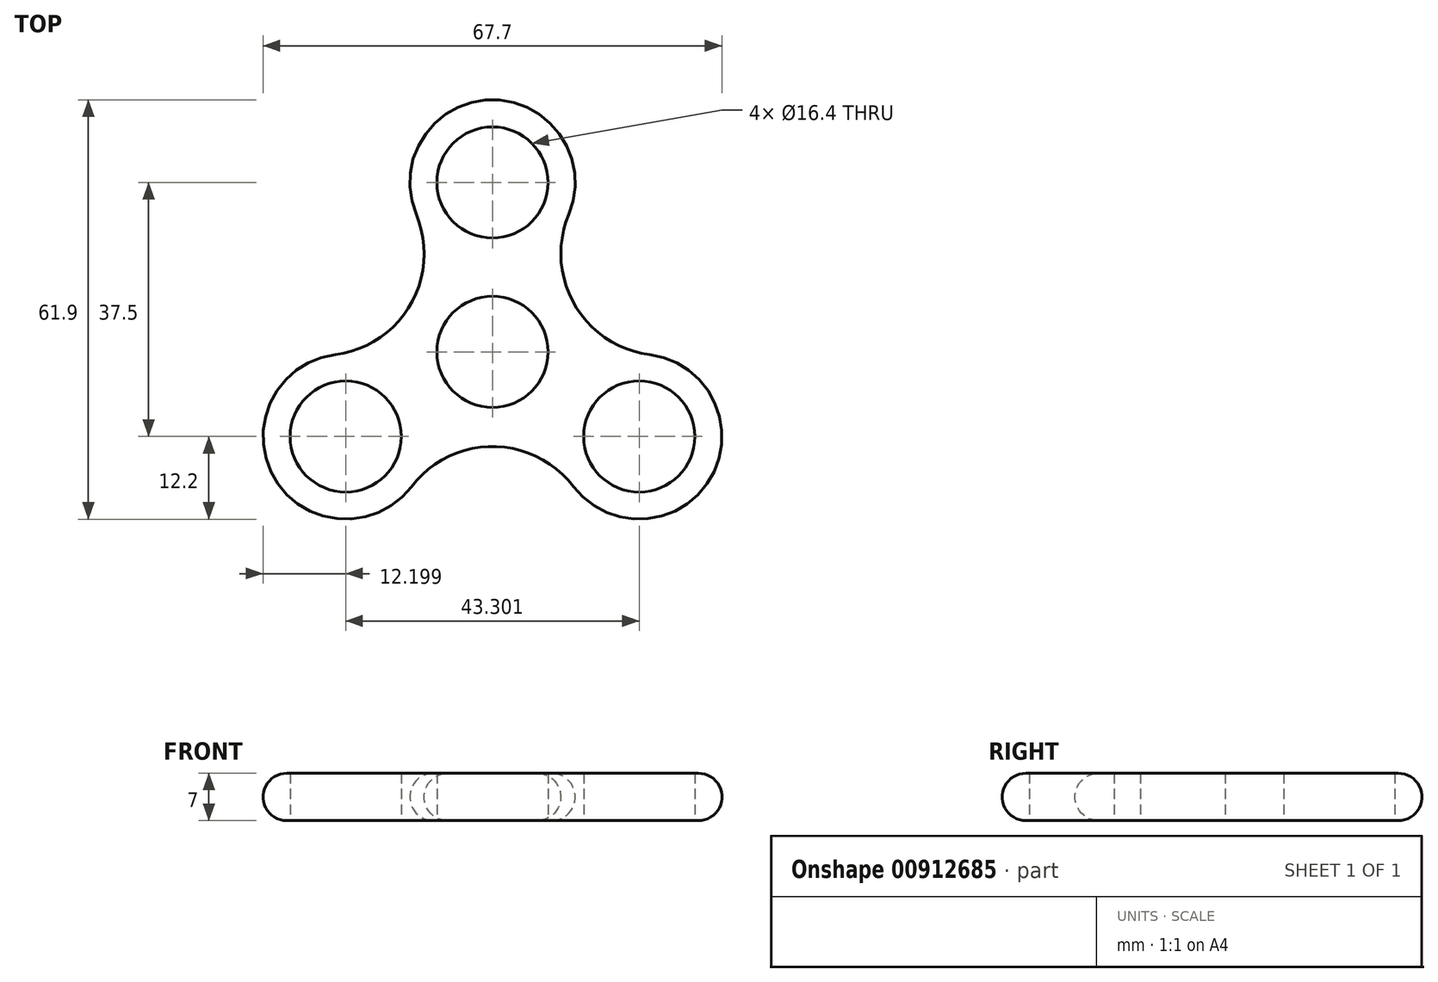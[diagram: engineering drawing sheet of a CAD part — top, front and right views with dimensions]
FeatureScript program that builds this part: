
annotation { "Feature Type Name" : "Feature", "Feature Type Description" : "" }
export const myFeature = defineFeature(function(context is Context, id is Id, definition is map)
    precondition{}
    {
        {
            var Q0;
            Q0=qCreatedBy(makeId("Top.planeOp"),FACE);
            var sketch = newSketch(context, id + "F0", { "sketchPlane" : qUnion([Q0])});
            skCircle(sketch, "E0", {"center": v(0, 25) * mm, "radius": 8.2 * mm});
            skCircle(sketch, "E1", {"center": v(21.65, -12.5) * mm, "radius": 8.2 * mm});
            skCircle(sketch, "E2", {"center": v(-21.65, -12.5) * mm, "radius": 8.2 * mm});
            skCircle(sketch, "E3", {"center": v(0, 0) * mm, "radius": 8.2 * mm});
            skArc(sketch, "E4", {"start": v(11.25, 20.28) * mm, "mid": v(12.1, 6.98) * mm, "end": v(23.2, -0.4) * mm});
            skArc(sketch, "E5", {"start": v(-23.2, -0.4) * mm, "mid": v(-12.1, 6.98) * mm, "end": v(-11.25, 20.28) * mm});
            skArc(sketch, "E6", {"start": v(11.94, -19.88) * mm, "mid": v(0, -13.96) * mm, "end": v(-11.94, -19.88) * mm});
            skCircle(sketch, "E7", {"center": v(0, 25) * mm, "radius": 12.2 * mm});
            skCircle(sketch, "E8", {"center": v(21.65, -12.5) * mm, "radius": 12.2 * mm});
            skCircle(sketch, "E9", {"center": v(-21.65, -12.5) * mm, "radius": 12.2 * mm});
            skLineSegment(sketch, "E10", {"start": v(0, 0) * mm, "end": v(-21.65, -12.5) * mm, "construction": true});
            skLineSegment(sketch, "E11", {"start": v(0, 0) * mm, "end": v(21.65, -12.5) * mm, "construction": true});
            skLineSegment(sketch, "E12", {"start": v(0, 0) * mm, "end": v(0, 25) * mm, "construction": true});
            skSolve(sketch);
        }
        {
            assignVariable(context, id + "F1", {"name" : "Altura", "anyValue" : 7 * mm});
        }
        {
            var Q0;
            {var subQ0=sQuery(id+"F0.wireOp",EDGE,"E9");var subQ1=sQuery(id+"F0.wireOp",EDGE,"AqzURDB5-sfJI-K8nH-HBUo-sjF5Fb8OYFWF");var subQ2=makeQuery(id+"F0.imprint","INTERSECT",VERTEX,{"disambiguationData":[OD(0.0)],"derivedFrom":[subQ1,subQ0]});Q0=makeQuery(id+"F0.imprint","IMPRINT",FACE,{"disambiguationData":[TD([[makeQuery(id+"F0.imprint","IMPRINT",EDGE,{"disambiguationData":[TD([[subQ2,-1.0]])],"derivedFrom":subQ1}),-1.0]])]});}
            var Q1;
            {var subQ0=sQuery(id+"F0.wireOp",EDGE,"E8");var subQ1=sQuery(id+"F0.wireOp",EDGE,"AqzURDB5-sfJI-K8nH-HBUo-sjF5Fb8OYFWF");var subQ2=makeQuery(id+"F0.imprint","INTERSECT",VERTEX,{"disambiguationData":[OD(1.0)],"derivedFrom":[subQ1,subQ0]});Q1=makeQuery(id+"F0.imprint","IMPRINT",FACE,{"disambiguationData":[TD([[makeQuery(id+"F0.imprint","IMPRINT",EDGE,{"disambiguationData":[TD([[subQ2,-1.0]])],"derivedFrom":subQ1}),-1.0]])]});}
            var Q2;
            {var subQ0=sQuery(id+"F0.wireOp",EDGE,"E7");var subQ1=sQuery(id+"F0.wireOp",EDGE,"AqzURDB5-sfJI-K8nH-HBUo-sjF5Fb8OYFWF");var subQ2=makeQuery(id+"F0.imprint","INTERSECT",VERTEX,{"disambiguationData":[OD(0.0)],"derivedFrom":[subQ1,subQ0]});Q2=makeQuery(id+"F0.imprint","IMPRINT",FACE,{"disambiguationData":[TD([[makeQuery(id+"F0.imprint","IMPRINT",EDGE,{"disambiguationData":[TD([[subQ2,-1.0]])],"derivedFrom":subQ1}),-1.0]])]});}
            var Q3;
            {var subQ0=sQuery(id+"F0.wireOp",EDGE,"E7");var subQ1=sQuery(id+"F0.wireOp",EDGE,"AqzURDB5-sfJI-K8nH-HBUo-sjF5Fb8OYFWF");var subQ2=makeQuery(id+"F0.imprint","INTERSECT",VERTEX,{"disambiguationData":[OD(0.0)],"derivedFrom":[subQ1,subQ0]});Q3=makeQuery(id+"F0.imprint","IMPRINT",FACE,{"disambiguationData":[TD([[makeQuery(id+"F0.imprint","IMPRINT",EDGE,{"disambiguationData":[TD([[subQ2,-1.0]])],"derivedFrom":subQ1}),1.0]])]});}
            var Q4;
            {var subQ0=sQuery(id+"F0.wireOp",EDGE,"MzTOxAbe-Fz2M-OVsh-RK3F-I7OQ9siJtZke");var subQ1=sQuery(id+"F0.wireOp",EDGE,"E0");var subQ2=makeQuery(id+"F0.imprint","INTERSECT",VERTEX,{"derivedFrom":[subQ1,subQ0]});Q4=makeQuery(id+"F0.imprint","IMPRINT",FACE,{"disambiguationData":[TD([[makeQuery(id+"F0.imprint","IMPRINT",EDGE,{"disambiguationData":[TD([[subQ2,-1.0]])],"derivedFrom":subQ1}),-1.0]])]});}
            var Q5;
            {var subQ0=sQuery(id+"F0.wireOp",EDGE,"E7");var subQ4=sQuery(id+"F0.wireOp",EDGE,"AqzURDB5-sfJI-K8nH-HBUo-sjF5Fb8OYFWF");var subQ5=makeQuery(id+"F0.imprint","INTERSECT",VERTEX,{"disambiguationData":[OD(1.0)],"derivedFrom":[subQ4,subQ0]});Q5=makeQuery(id+"F0.imprint","IMPRINT",FACE,{"disambiguationData":[TD([[makeQuery(id+"F0.imprint","IMPRINT",EDGE,{"disambiguationData":[TD([[subQ5,1.0]])],"derivedFrom":subQ4}),1.0]])]});}
            var Q6;
            {var subQ0=sQuery(id+"F0.wireOp",EDGE,"E7");var subQ1=sQuery(id+"F0.wireOp",EDGE,"E5");var subQ2=makeQuery(id+"F0.imprint","INTERSECT",VERTEX,{"derivedFrom":[subQ1,subQ0]});Q6=makeQuery(id+"F0.imprint","IMPRINT",FACE,{"disambiguationData":[TD([[makeQuery(id+"F0.imprint","IMPRINT",EDGE,{"disambiguationData":[TD([[subQ2,1.0]])],"derivedFrom":subQ1}),-1.0]])]});}
            var Q7;
            Q7=makeQuery(id+"F0.imprint","IMPRINT",FACE,{"disambiguationData":[TD([[makeQuery(id+"F0.imprint","IMPRINT",EDGE,{"derivedFrom":sQuery(id+"F0.wireOp",EDGE,"E3")}),-1.0]])]});
            var Q8;
            {var subQ0=sQuery(id+"F0.wireOp",EDGE,"E7");var subQ1=sQuery(id+"F0.wireOp",EDGE,"E4");var subQ2=makeQuery(id+"F0.imprint","INTERSECT",VERTEX,{"derivedFrom":[subQ1,subQ0]});Q8=makeQuery(id+"F0.imprint","IMPRINT",FACE,{"disambiguationData":[TD([[makeQuery(id+"F0.imprint","IMPRINT",EDGE,{"disambiguationData":[TD([[subQ2,-1.0]])],"derivedFrom":subQ1}),-1.0]])]});}
            var Q9;
            {var subQ0=sQuery(id+"F0.wireOp",EDGE,"E8");var subQ1=sQuery(id+"F0.wireOp",EDGE,"E6");var subQ2=makeQuery(id+"F0.imprint","INTERSECT",VERTEX,{"derivedFrom":[subQ1,subQ0]});Q9=makeQuery(id+"F0.imprint","IMPRINT",FACE,{"disambiguationData":[TD([[makeQuery(id+"F0.imprint","IMPRINT",EDGE,{"disambiguationData":[TD([[subQ2,-1.0]])],"derivedFrom":subQ1}),-1.0]])]});}
            var Q10;
            {var subQ0=sQuery(id+"F0.wireOp",EDGE,"E8");var subQ1=sQuery(id+"F0.wireOp",EDGE,"AqzURDB5-sfJI-K8nH-HBUo-sjF5Fb8OYFWF");var subQ2=makeQuery(id+"F0.imprint","INTERSECT",VERTEX,{"disambiguationData":[OD(1.0)],"derivedFrom":[subQ1,subQ0]});Q10=makeQuery(id+"F0.imprint","IMPRINT",FACE,{"disambiguationData":[TD([[makeQuery(id+"F0.imprint","IMPRINT",EDGE,{"disambiguationData":[TD([[subQ2,-1.0]])],"derivedFrom":subQ1}),1.0]])]});}
            var Q11;
            {var subQ0=sQuery(id+"F0.wireOp",EDGE,"E8");var subQ4=sQuery(id+"F0.wireOp",EDGE,"AqzURDB5-sfJI-K8nH-HBUo-sjF5Fb8OYFWF");var subQ5=makeQuery(id+"F0.imprint","INTERSECT",VERTEX,{"disambiguationData":[OD(0.0)],"derivedFrom":[subQ4,subQ0]});Q11=makeQuery(id+"F0.imprint","IMPRINT",FACE,{"disambiguationData":[TD([[makeQuery(id+"F0.imprint","IMPRINT",EDGE,{"disambiguationData":[TD([[subQ5,1.0]])],"derivedFrom":subQ4}),1.0]])]});}
            var Q12;
            {var subQ0=sQuery(id+"F0.wireOp",EDGE,"OnGKlqgY-9iZ4-aYWp-Duck-tBlSKBJGLVlU");var subQ1=sQuery(id+"F0.wireOp",EDGE,"E1");var subQ2=makeQuery(id+"F0.imprint","INTERSECT",VERTEX,{"derivedFrom":[subQ1,subQ0]});Q12=makeQuery(id+"F0.imprint","IMPRINT",FACE,{"disambiguationData":[TD([[makeQuery(id+"F0.imprint","IMPRINT",EDGE,{"disambiguationData":[TD([[subQ2,-1.0]])],"derivedFrom":subQ1}),-1.0]])]});}
            var Q13;
            {var subQ0=sQuery(id+"F0.wireOp",EDGE,"MzTOxAbe-Fz2M-OVsh-RK3F-I7OQ9siJtZke");var subQ1=sQuery(id+"F0.wireOp",EDGE,"E2");var subQ2=makeQuery(id+"F0.imprint","INTERSECT",VERTEX,{"derivedFrom":[subQ1,subQ0]});Q13=makeQuery(id+"F0.imprint","IMPRINT",FACE,{"disambiguationData":[TD([[makeQuery(id+"F0.imprint","IMPRINT",EDGE,{"disambiguationData":[TD([[subQ2,1.0]])],"derivedFrom":subQ1}),-1.0]])]});}
            var Q14;
            {var subQ0=sQuery(id+"F0.wireOp",EDGE,"E9");var subQ4=sQuery(id+"F0.wireOp",EDGE,"AqzURDB5-sfJI-K8nH-HBUo-sjF5Fb8OYFWF");var subQ5=makeQuery(id+"F0.imprint","INTERSECT",VERTEX,{"disambiguationData":[OD(0.0)],"derivedFrom":[subQ4,subQ0]});Q14=makeQuery(id+"F0.imprint","IMPRINT",FACE,{"disambiguationData":[TD([[makeQuery(id+"F0.imprint","IMPRINT",EDGE,{"disambiguationData":[TD([[subQ5,-1.0]])],"derivedFrom":subQ4}),1.0]])]});}
            var Q15;
            {var subQ0=sQuery(id+"F0.wireOp",EDGE,"E9");var subQ1=sQuery(id+"F0.wireOp",EDGE,"AqzURDB5-sfJI-K8nH-HBUo-sjF5Fb8OYFWF");var subQ2=makeQuery(id+"F0.imprint","INTERSECT",VERTEX,{"disambiguationData":[OD(1.0)],"derivedFrom":[subQ1,subQ0]});Q15=makeQuery(id+"F0.imprint","IMPRINT",FACE,{"disambiguationData":[TD([[makeQuery(id+"F0.imprint","IMPRINT",EDGE,{"disambiguationData":[TD([[subQ2,1.0]])],"derivedFrom":subQ1}),1.0]])]});}
            var Q16;
            {var subQ1=sQuery(id+"F0.wireOp",EDGE,"AqzURDB5-sfJI-K8nH-HBUo-sjF5Fb8OYFWF");var subQ6=sQuery(id+"F0.wireOp",EDGE,"E7");var subQ7=makeQuery(id+"F0.imprint","INTERSECT",VERTEX,{"disambiguationData":[OD(1.0)],"derivedFrom":[subQ1,subQ6]});Q16=makeQuery(id+"F0.imprint","IMPRINT",FACE,{"disambiguationData":[TD([[makeQuery(id+"F0.imprint","IMPRINT",EDGE,{"disambiguationData":[TD([[subQ7,-1.0]])],"derivedFrom":subQ1}),1.0]])]});}
            var Q17;
            {var subQ1=sQuery(id+"F0.wireOp",EDGE,"AqzURDB5-sfJI-K8nH-HBUo-sjF5Fb8OYFWF");var subQ5=sQuery(id+"F0.wireOp",EDGE,"E4");var subQ7=makeQuery(id+"F0.imprint","INTERSECT",VERTEX,{"disambiguationData":[OD(0.0)],"derivedFrom":[subQ1,subQ5]});Q17=makeQuery(id+"F0.imprint","IMPRINT",FACE,{"disambiguationData":[TD([[makeQuery(id+"F0.imprint","IMPRINT",EDGE,{"disambiguationData":[TD([[subQ7,1.0]])],"derivedFrom":subQ1}),1.0]])]});}
            var Q18;
            {var subQ1=sQuery(id+"F0.wireOp",EDGE,"AqzURDB5-sfJI-K8nH-HBUo-sjF5Fb8OYFWF");var subQ8=sQuery(id+"F0.wireOp",EDGE,"E9");var subQ10=makeQuery(id+"F0.imprint","INTERSECT",VERTEX,{"disambiguationData":[OD(1.0)],"derivedFrom":[subQ1,subQ8]});Q18=makeQuery(id+"F0.imprint","IMPRINT",FACE,{"disambiguationData":[TD([[makeQuery(id+"F0.imprint","IMPRINT",EDGE,{"disambiguationData":[TD([[subQ10,-1.0]])],"derivedFrom":subQ1}),1.0]])]});}
            extrude(context, id + "F2", {"entities" : qUnion([Q0, Q1, Q2, Q3, Q4, Q5, Q6, Q7, Q8, Q9, Q10, Q11, Q12, Q13, Q14, Q15, Q16, Q17, Q18]), "depth" : getVariable(context, 'Altura'), "offsetDistance" : 25 * mm});
        }
        {
            var Q0;
            Q0=makeQuery(id+"F2.opExtrude","SWEPT_FACE",FACE,{"disambiguationData":[OSD([sQuery(id+"F0.wireOp",EDGE,"E9")])]});
            var Q1;
            Q1=makeQuery(id+"F2.opExtrude","SWEPT_FACE",FACE,{"disambiguationData":[OSD([sQuery(id+"F0.wireOp",EDGE,"E6")])]});
            var Q2;
            Q2=makeQuery(id+"F2.opExtrude","SWEPT_FACE",FACE,{"disambiguationData":[OSD([sQuery(id+"F0.wireOp",EDGE,"E8")])]});
            var Q3;
            Q3=makeQuery(id+"F2.opExtrude","SWEPT_FACE",FACE,{"disambiguationData":[OSD([sQuery(id+"F0.wireOp",EDGE,"E4")])]});
            var Q4;
            Q4=makeQuery(id+"F2.opExtrude","SWEPT_FACE",FACE,{"disambiguationData":[OSD([sQuery(id+"F0.wireOp",EDGE,"E7")])]});
            var Q5;
            Q5=makeQuery(id+"F2.opExtrude","SWEPT_FACE",FACE,{"disambiguationData":[OSD([sQuery(id+"F0.wireOp",EDGE,"E5")])]});
            fillet(context, id + "F3", {"entities" : qUnion([Q0, Q1, Q2, Q3, Q4, Q5]), "radius" : getVariable(context, 'Altura') / 2, "tangentPropagation" : true, "allowEdgeOverflow" : false});
        }
    });
